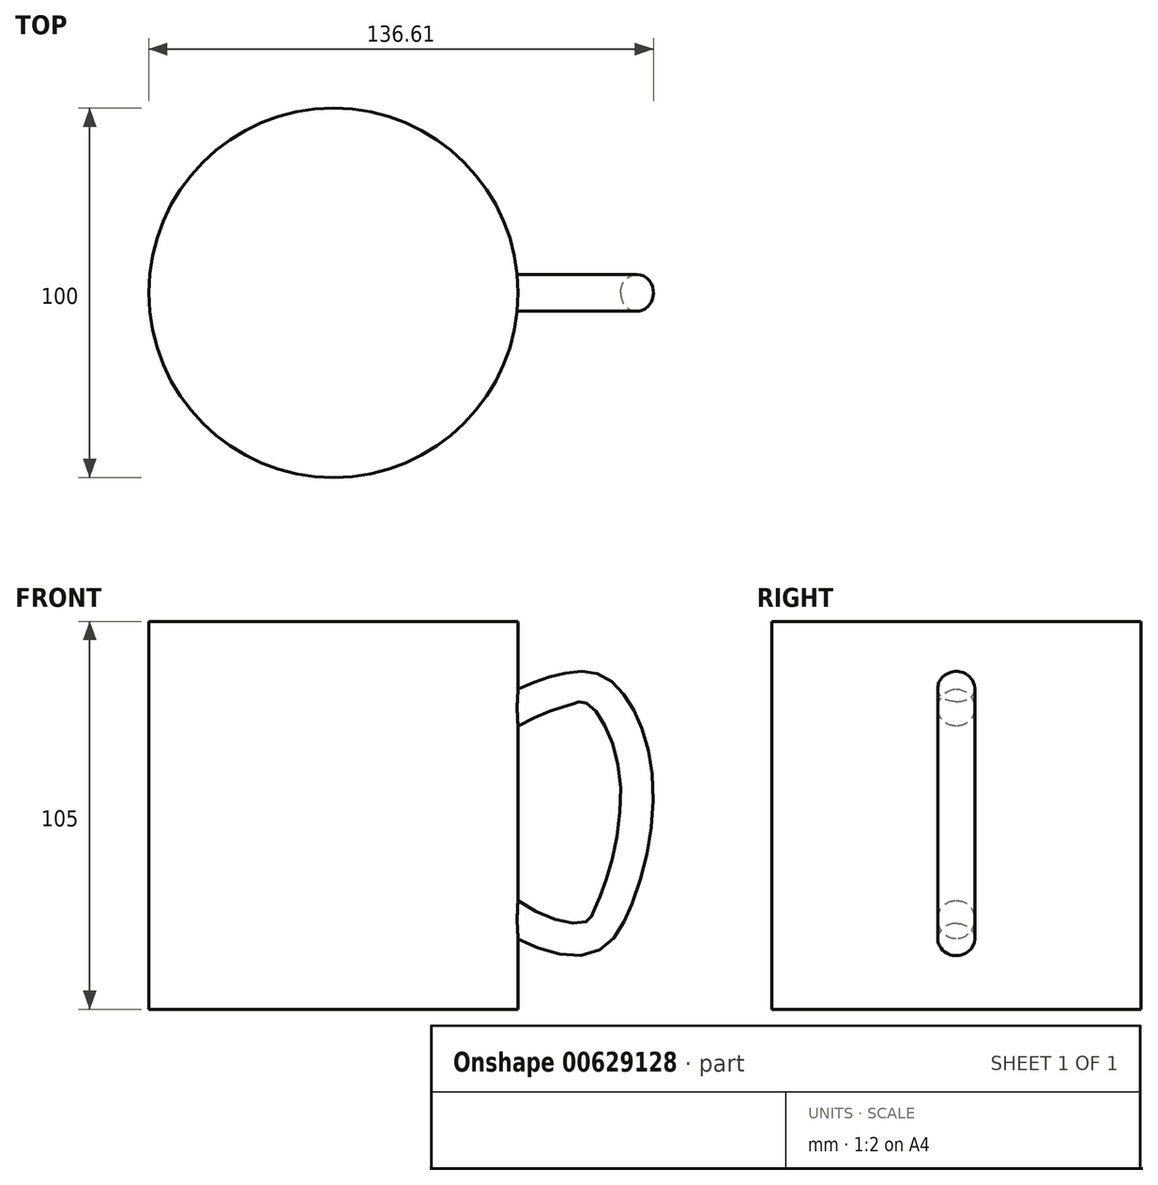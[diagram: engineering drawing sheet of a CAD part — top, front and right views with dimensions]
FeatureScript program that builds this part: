
annotation { "Feature Type Name" : "Feature", "Feature Type Description" : "" }
export const myFeature = defineFeature(function(context is Context, id is Id, definition is map)
    precondition{}
    {
        {
            var Q0;
            Q0=qCreatedBy(makeId("Top.planeOp"),FACE);
            var sketch = newSketch(context, id + "F0", { "sketchPlane" : qUnion([Q0])});
            skCircle(sketch, "E0", {"center": v(0, 0) * mm, "radius": 50 * mm});
            skSolve(sketch);
        }
        {
            var Q0;
            Q0 = qSketchRegion(id + "F0", true);
            extrude(context, id + "F1", {"entities" : qUnion([Q0]), "depth" : 105 * mm, "offsetDistance" : 25 * mm});
        }
        {
            var Q0;
            Q0=qCreatedBy(makeId("Front.planeOp"),FACE);
            var sketch = newSketch(context, id + "F2", { "sketchPlane" : qUnion([Q0])});
            skFitSpline(sketch, "E1", {"points": [v(43.9, 78.85) * mm, v(63.74, 87.35) * mm, v(73.18, 85.46) * mm, v(82.63, 62.8) * mm, v(76.49, 27.86) * mm, v(66.57, 18.41) * mm, v(42.02, 29.75) * mm], "startDerivative": vector(119, 81.73) * mm, "endDerivative": vector(-105, 112.08) * mm});
            skSolve(sketch);
        }
        {
            var Q0;
            Q0=qCreatedBy(makeId("Right.planeOp"),FACE);
            cPlane(context, id + "F3", {"entities" : qUnion([Q0]), "cplaneType" : CPlaneType.OFFSET, "offset" : 50 * mm, "width" : 150 * mm, "height" : 150 * mm});
        }
        {
            var Q0;
            Q0=qCreatedBy(id+"F3.planeOp",FACE);
            var sketch = newSketch(context, id + "F4", { "sketchPlane" : qUnion([Q0])});
            skCircle(sketch, "E2", {"center": v(0, 81.68) * mm, "radius": 5 * mm});
            skSolve(sketch);
        }
        {
            var Q0;
            Q0 = qSketchRegion(id + "F4", true);
            var Q1;
            Q1=sQuery(id+"F2.wireOp",EDGE,"E1");
            sweep(context, id + "F5", {"operationType" : NewBodyOperationType.ADD, "profiles" : qUnion([Q0]), "path" : qUnion([Q1])});
        }
    });
